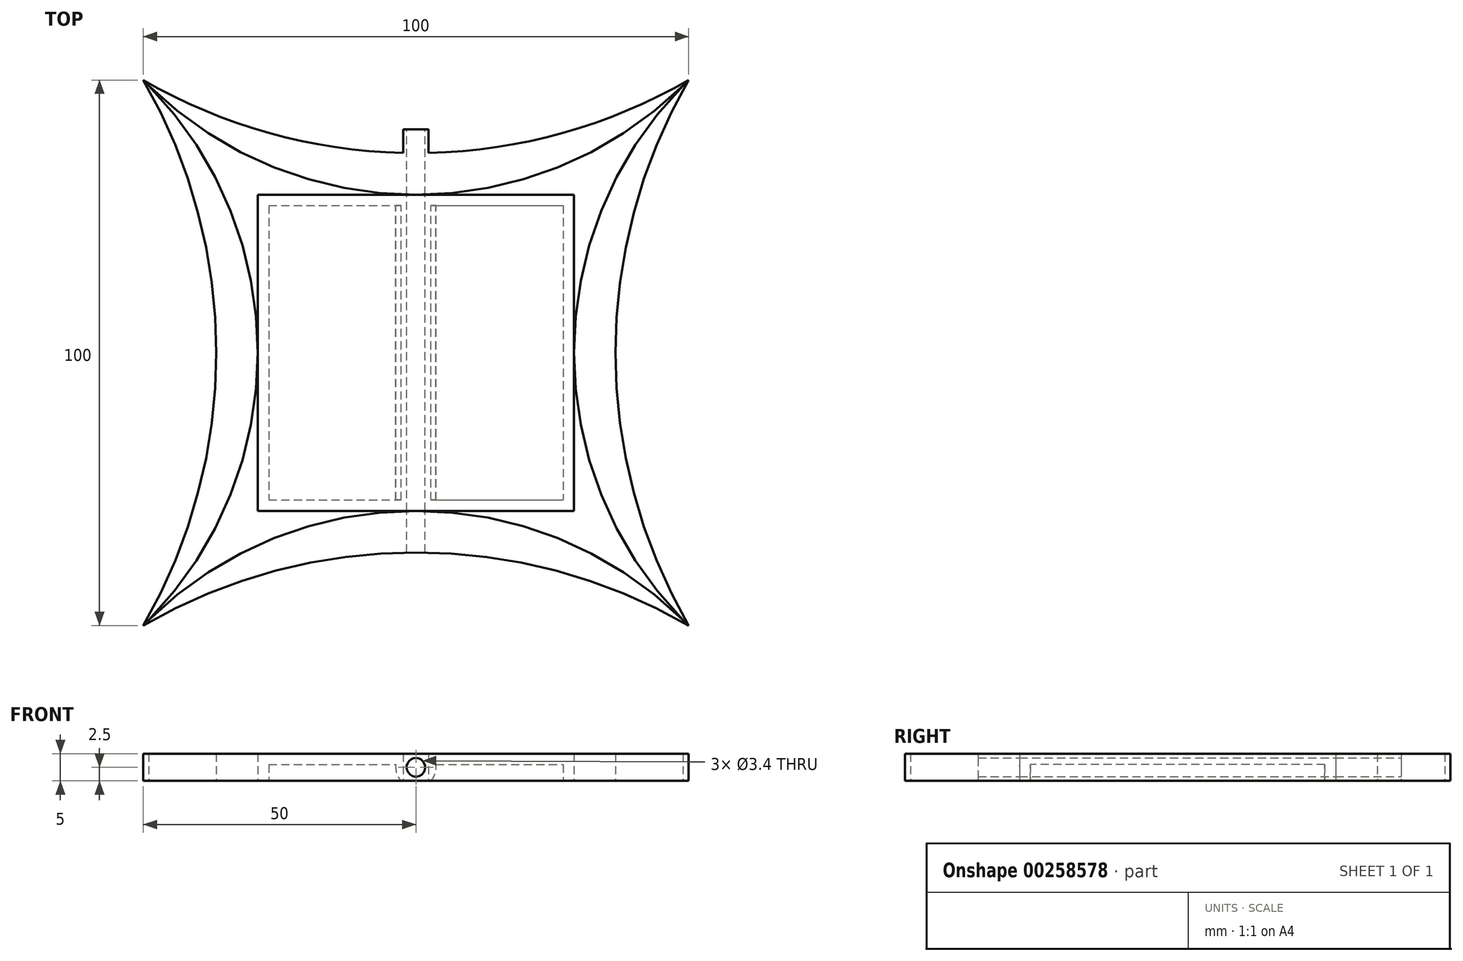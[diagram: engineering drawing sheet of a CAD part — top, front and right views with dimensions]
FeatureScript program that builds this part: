
annotation { "Feature Type Name" : "Feature", "Feature Type Description" : "" }
export const myFeature = defineFeature(function(context is Context, id is Id, definition is map)
    precondition{}
    {
        {
            var Q0;
            Q0=qCreatedBy(makeId("Top.planeOp"),FACE);
            var sketch = newSketch(context, id + "F0", { "sketchPlane" : qUnion([Q0])});
            skLineSegment(sketch, "E0.bottom", {"start": v(50, -50) * mm, "end": v(-50, -50) * mm});
            skLineSegment(sketch, "E0.top", {"start": v(50, 50) * mm, "end": v(-50, 50) * mm});
            skLineSegment(sketch, "E0.left", {"start": v(50, -50) * mm, "end": v(50, 50) * mm});
            skLineSegment(sketch, "E0.right", {"start": v(-50, -50) * mm, "end": v(-50, 50) * mm});
            skPoint(sketch, "E0.middle", {"position": v(0, 0) * mm});
            skArc(sketch, "E1", {"start": v(-50, -50) * mm, "mid": v(-36.6, 0) * mm, "end": v(-50, 50) * mm});
            skArc(sketch, "E2", {"start": v(-50, 50) * mm, "mid": v(0, 36.6) * mm, "end": v(50, 50) * mm});
            skArc(sketch, "E3", {"start": v(50, 50) * mm, "mid": v(36.6, 0) * mm, "end": v(50, -50) * mm});
            skArc(sketch, "E4", {"start": v(50, -50) * mm, "mid": v(0, -36.6) * mm, "end": v(-50, -50) * mm});
            skPoint(sketch, "E5", {"position": v(-36.6, 0) * mm});
            skPoint(sketch, "E6", {"position": v(36.6, 0) * mm});
            skArc(sketch, "E7", {"start": v(-50, 50) * mm, "mid": v(0, 28.99) * mm, "end": v(50, 50) * mm});
            skArc(sketch, "E8", {"start": v(-50, -50) * mm, "mid": v(-28.99, 0) * mm, "end": v(-50, 50) * mm});
            skArc(sketch, "E9", {"start": v(50, -50) * mm, "mid": v(0, -28.99) * mm, "end": v(-50, -50) * mm});
            skArc(sketch, "E10", {"start": v(50, 50) * mm, "mid": v(28.99, 0) * mm, "end": v(50, -50) * mm});
            skPoint(sketch, "E11", {"position": v(-28.99, 0) * mm});
            skPoint(sketch, "E12", {"position": v(28.99, 0) * mm});
            skLineSegment(sketch, "E13.left", {"start": v(2.33, 41) * mm, "end": v(2.33, 41) * mm});
            skLineSegment(sketch, "E13.right", {"start": v(-13.9, 41) * mm, "end": v(-13.9, 41) * mm});
            skPoint(sketch, "E13.middle", {"position": v(-5.79, 41) * mm});
            skPoint(sketch, "E14.middle", {"position": v(0, 41) * mm});
            skPoint(sketch, "E15.orphan", {"position": v(-29.32, 41) * mm});
            skPoint(sketch, "E16.trimOffspring.end.orphan", {"position": v(4.38, 35) * mm});
            skPoint(sketch, "E17.trimOffspring.end.orphan", {"position": v(-4.38, 35) * mm});
            skPoint(sketch, "E14.bottom.end.orphan", {"position": v(-4.38, 47) * mm});
            skPoint(sketch, "E14.bottom.start.orphan", {"position": v(4.38, 47) * mm});
            skPoint(sketch, "E18.trimOffspring.end.orphan", {"position": v(29.32, 41) * mm});
            skPoint(sketch, "E19.bottom.end.orphan", {"position": v(-29.32, -41) * mm});
            skPoint(sketch, "E19.left.start.orphan", {"position": v(29.32, -41) * mm});
            skPoint(sketch, "E20.firstSnap0", {"position": v(0, 28.99) * mm});
            skPoint(sketch, "E20.oppositeSnap0", {"position": v(0, -28.99) * mm});
            skLineSegment(sketch, "E20.bottom", {"start": v(-28.99, 28.99) * mm, "end": v(28.99, 28.99) * mm});
            skLineSegment(sketch, "E20.top", {"start": v(-28.99, -28.99) * mm, "end": v(28.99, -28.99) * mm});
            skLineSegment(sketch, "E20.left", {"start": v(-28.99, 28.99) * mm, "end": v(-28.99, -28.99) * mm});
            skLineSegment(sketch, "E20.right", {"start": v(28.99, 28.99) * mm, "end": v(28.99, -28.99) * mm});
            skLineSegment(sketch, "E21.bottom", {"start": v(-2.33, 28.99) * mm, "end": v(2.33, 28.99) * mm});
            skLineSegment(sketch, "E21.top", {"start": v(-2.33, 41) * mm, "end": v(2.33, 41) * mm});
            skLineSegment(sketch, "E21.left", {"start": v(-2.33, 28.99) * mm, "end": v(-2.33, 41) * mm});
            skLineSegment(sketch, "E21.right", {"start": v(2.33, 28.99) * mm, "end": v(2.33, 41) * mm});
            skSolve(sketch);
        }
        {
            var Q0;
            {var subQ0=sQuery(id+"F0.wireOp",EDGE,"E21.left");var subQ1=sQuery(id+"F0.wireOp",EDGE,"E2");var subQ2=makeQuery(id+"F0.imprint","INTERSECT",VERTEX,{"derivedFrom":[subQ1,subQ0]});Q0=makeQuery(id+"F0.imprint","IMPRINT",FACE,{"disambiguationData":[TD([[makeQuery(id+"F0.imprint","IMPRINT",EDGE,{"disambiguationData":[TD([[subQ2,-1.0]])],"derivedFrom":subQ1}),-1.0]])]});}
            var Q1;
            {var subQ0=sQuery(id+"F0.wireOp",EDGE,"E8");var subQ1=sQuery(id+"F0.wireOp",EDGE,"E7");var subQ7=makeQuery(id+"F0.imprint","INTERSECT",VERTEX,{"derivedFrom":[subQ1,subQ0]});Q1=makeQuery(id+"F0.imprint","IMPRINT",FACE,{"disambiguationData":[TD([[makeQuery(id+"F0.imprint","IMPRINT",EDGE,{"disambiguationData":[TD([[subQ7,-1.0]])],"derivedFrom":subQ1}),1.0]])]});}
            var Q2;
            {var subQ1=sQuery(id+"F0.wireOp",EDGE,"E7");var subQ4=sQuery(id+"F0.wireOp",EDGE,"E21.right");var subQ6=makeQuery(id+"F0.imprint","INTERSECT",VERTEX,{"derivedFrom":[subQ1,subQ4]});Q2=makeQuery(id+"F0.imprint","IMPRINT",FACE,{"disambiguationData":[TD([[makeQuery(id+"F0.imprint","IMPRINT",EDGE,{"disambiguationData":[TD([[subQ6,-1.0]])],"derivedFrom":subQ1}),1.0]])]});}
            var Q3;
            {var subQ5=sQuery(id+"F0.wireOp",EDGE,"E21.top");Q3=makeQuery(id+"F0.imprint","IMPRINT",FACE,{"disambiguationData":[TD([[makeQuery(id+"F0.imprint","IMPRINT",EDGE,{"derivedFrom":subQ5}),-1.0]])]});}
            var Q4;
            {var subQ1=sQuery(id+"F0.wireOp",EDGE,"E20.top");var subQ4=sQuery(id+"F0.wireOp",EDGE,"E20.left");var subQ5=makeQuery(id+"F0.imprint","INTERSECT",VERTEX,{"derivedFrom":[subQ1,subQ4]});Q4=makeQuery(id+"F0.imprint","IMPRINT",FACE,{"disambiguationData":[TD([[makeQuery(id+"F0.imprint","IMPRINT",EDGE,{"disambiguationData":[TD([[subQ5,-1.0]])],"derivedFrom":subQ1}),1.0]])]});}
            var Q5;
            {var subQ6=sQuery(id+"F0.wireOp",EDGE,"E1");Q5=makeQuery(id+"F0.imprint","IMPRINT",FACE,{"disambiguationData":[TD([[makeQuery(id+"F0.imprint","IMPRINT",EDGE,{"derivedFrom":subQ6}),-1.0]])]});}
            var Q6;
            {var subQ6=sQuery(id+"F0.wireOp",EDGE,"E4");Q6=makeQuery(id+"F0.imprint","IMPRINT",FACE,{"disambiguationData":[TD([[makeQuery(id+"F0.imprint","IMPRINT",EDGE,{"derivedFrom":subQ6}),-1.0]])]});}
            var Q7;
            {var subQ5=sQuery(id+"F0.wireOp",EDGE,"E3");Q7=makeQuery(id+"F0.imprint","IMPRINT",FACE,{"disambiguationData":[TD([[makeQuery(id+"F0.imprint","IMPRINT",EDGE,{"derivedFrom":subQ5}),-1.0]])]});}
            extrude(context, id + "F1", {"entities" : qUnion([Q0, Q1, Q2, Q3, Q4, Q5, Q6, Q7]), "depth" : 5 * mm});
        }
        {
            var Q0;
            Q0=makeQuery(id+"F1.opExtrude","SWEPT_FACE",FACE,{"disambiguationData":[OSD([sQuery(id+"F0.wireOp",EDGE,"E21.top")])]});
            var sketch = newSketch(context, id + "F2", { "sketchPlane" : qUnion([Q0])});
            skLineSegment(sketch, "E22", {"start": v(0, 5) * mm, "end": v(0, 0) * mm});
            skLineSegment(sketch, "E23", {"start": v(0, 0) * mm, "end": v(0, 5) * mm});
            skCircle(sketch, "E24", {"center": v(0, 2.5) * mm, "radius": 1.7 * mm});
            skSolve(sketch);
        }
        {
            var Q0;
            Q0 = qSketchRegion(id + "F2", true);
            var Q1;
            Q1=makeQuery(id+"FRi0DV2lXjglq9K_5.opShell","OFFSET_FACE",FACE,{"disambiguationData":[OSD([sQuery(id+"F0.wireOp",EDGE,"E20.top")])]});
            extrude(context, id + "F3", {"entities" : qUnion([Q0, Q1]), "operationType" : NewBodyOperationType.REMOVE, "oppositeDirection" : true, "depth" : 100 * mm});
        }
        {
            var Q0;
            Q0=makeQuery(id+"F1.opExtrude","CAP_FACE",FACE,{"disambiguationData":[OSD([sQuery(id+"F0.wireOp",EDGE,"E20.bottom"),sQuery(id+"F0.wireOp",EDGE,"E20.top"),sQuery(id+"F0.wireOp",EDGE,"E20.left"),sQuery(id+"F0.wireOp",EDGE,"E20.right"),sQuery(id+"F0.wireOp",EDGE,"E21.bottom")])],"isStart":true});
            shell(context, id + "F4", {"entities" : qUnion([Q0]), "thickness" : 2 * mm});
        }
    });
